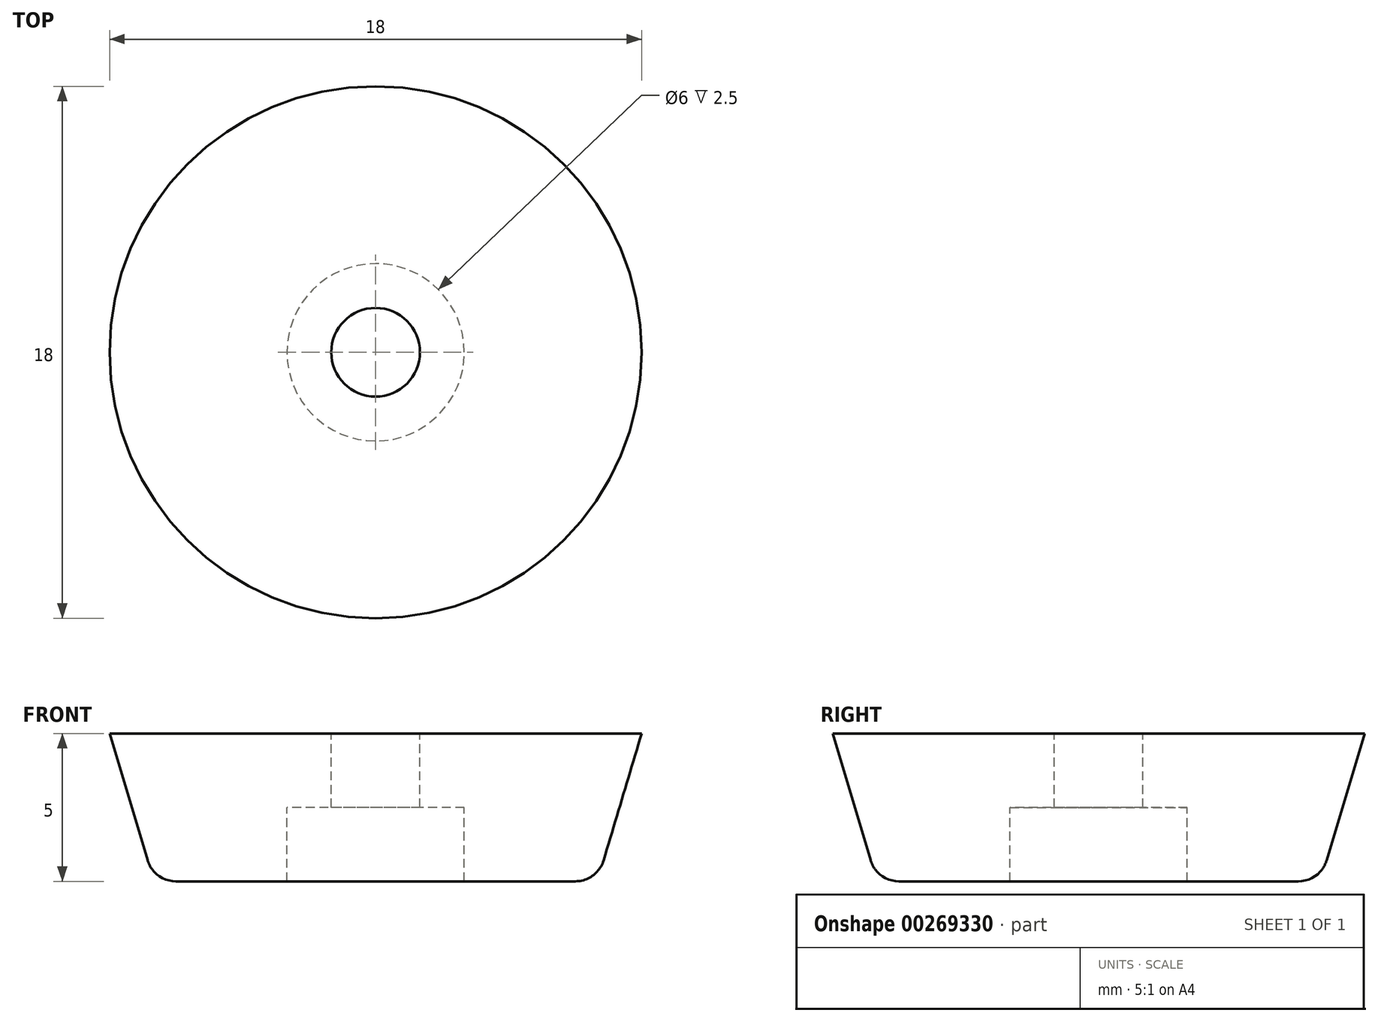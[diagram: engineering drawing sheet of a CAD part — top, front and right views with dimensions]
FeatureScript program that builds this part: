
annotation { "Feature Type Name" : "Feature", "Feature Type Description" : "" }
export const myFeature = defineFeature(function(context is Context, id is Id, definition is map)
    precondition{}
    {
        {
            var Q0;
            Q0=qCreatedBy(makeId("Front.planeOp"),FACE);
            var sketch = newSketch(context, id + "F0", { "sketchPlane" : qUnion([Q0])});
            skLineSegment(sketch, "E0", {"start": v(1.5, 0) * mm, "end": v(1.5, -2.5) * mm});
            skLineSegment(sketch, "E1", {"start": v(1.5, -2.5) * mm, "end": v(3, -2.5) * mm});
            skLineSegment(sketch, "E2", {"start": v(3, -2.5) * mm, "end": v(3, -5) * mm});
            skLineSegment(sketch, "E3", {"start": v(3, -5) * mm, "end": v(6.76, -5) * mm});
            skLineSegment(sketch, "E4", {"start": v(7.71, -4.29) * mm, "end": v(9, 0) * mm});
            skLineSegment(sketch, "E5", {"start": v(9, 0) * mm, "end": v(1.5, 0) * mm});
            skLineSegment(sketch, "E6", {"start": v(0, 0) * mm, "end": v(0, -5) * mm, "construction": true});
            skPoint(sketch, "E7.visualSharp", {"position": v(7.5, -5) * mm});
            skArc(sketch, "E7.filletArc", {"start": v(6.76, -5) * mm, "mid": v(7.35, -4.8) * mm, "end": v(7.71, -4.29) * mm});
            skSolve(sketch);
        }
        {
            var Q0;
            Q0=makeQuery(id+"F0.imprint","IMPRINT",FACE,{"disambiguationData":[TD([[makeQuery(id+"F0.imprint","IMPRINT",EDGE,{"derivedFrom":sQuery(id+"F0.wireOp",EDGE,"E0")}),1.0]])]});
            var Q1;
            Q1=sQuery(id+"F0.wireOp",EDGE,"E6");
            revolve(context, id + "F1", {"entities" : qUnion([Q0]), "axis" : qUnion([Q1]), "revolveType" : RevolveType.FULL});
        }
    });
